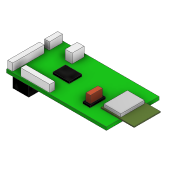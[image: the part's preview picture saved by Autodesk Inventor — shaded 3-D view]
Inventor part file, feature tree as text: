
AUTODESK INVENTOR PART (.ipt)
format: ipt  version: 2022.3 (Build 263350000, 350)  size: 181,760 bytes
history: native  units: mm
features: extrude x8, sketch x8, other x1
ambient origin geometry x8: Origin, YZ Plane, XZ Plane, XY Plane, X Axis, Y Axis, Z Axis, Center Point
bodies: Body1 (feature_tree)
feature tree (17):
  other  "Sólido1"
  extrude  "Extrusión1"  Depth=26.3mm
  extrude  "Extrusión2"  Depth=0.5mm TaperAngle=0.0deg
  extrude  "Extrusión3"  Depth=3.7mm TaperAngle=0.0deg
  extrude  "Extrusión4"  Depth=4.7mm TaperAngle=0.0deg
  extrude  "Extrusión5"  Depth=2.5mm
  extrude  "Extrusión6"  Depth=8.0mm
  extrude  "Extrusión7"  Depth=25.0mm
  extrude  "Extrusión8"  [1 undecoded]
  sketch  "Boceto1"  dims[d0=50.0mm d1=26.3mm]
  sketch  "Boceto2"  dims[d2=1.6mm d3=0.0mm d4=0.5mm d5=0.0mm]
  sketch  "Boceto3"  dims[d6=1.5mm d7=0.0mm d8=3.7mm d9=0.0mm]
  sketch  "Boceto4"  dims[d10=1.0mm d11=0.0mm d12=4.7mm d13=0.0mm]
  sketch  "Boceto5"  dims[d14=3.7mm d15=0.0mm d16=2.5mm]
  sketch  "Boceto6"  dims[d17=12.5mm d18=8.0mm]
  sketch  "Boceto7"  dims[d19=0.0mm d20=25.0mm]
  sketch  "Boceto8"  dims[d21=5.7mm d22=0.0mm]
note: 1 required parameter value undecoded (feature->parameter linkage not recoverable at this tier; creation-order binding heuristic only, values carry confidence <= 0.55)
